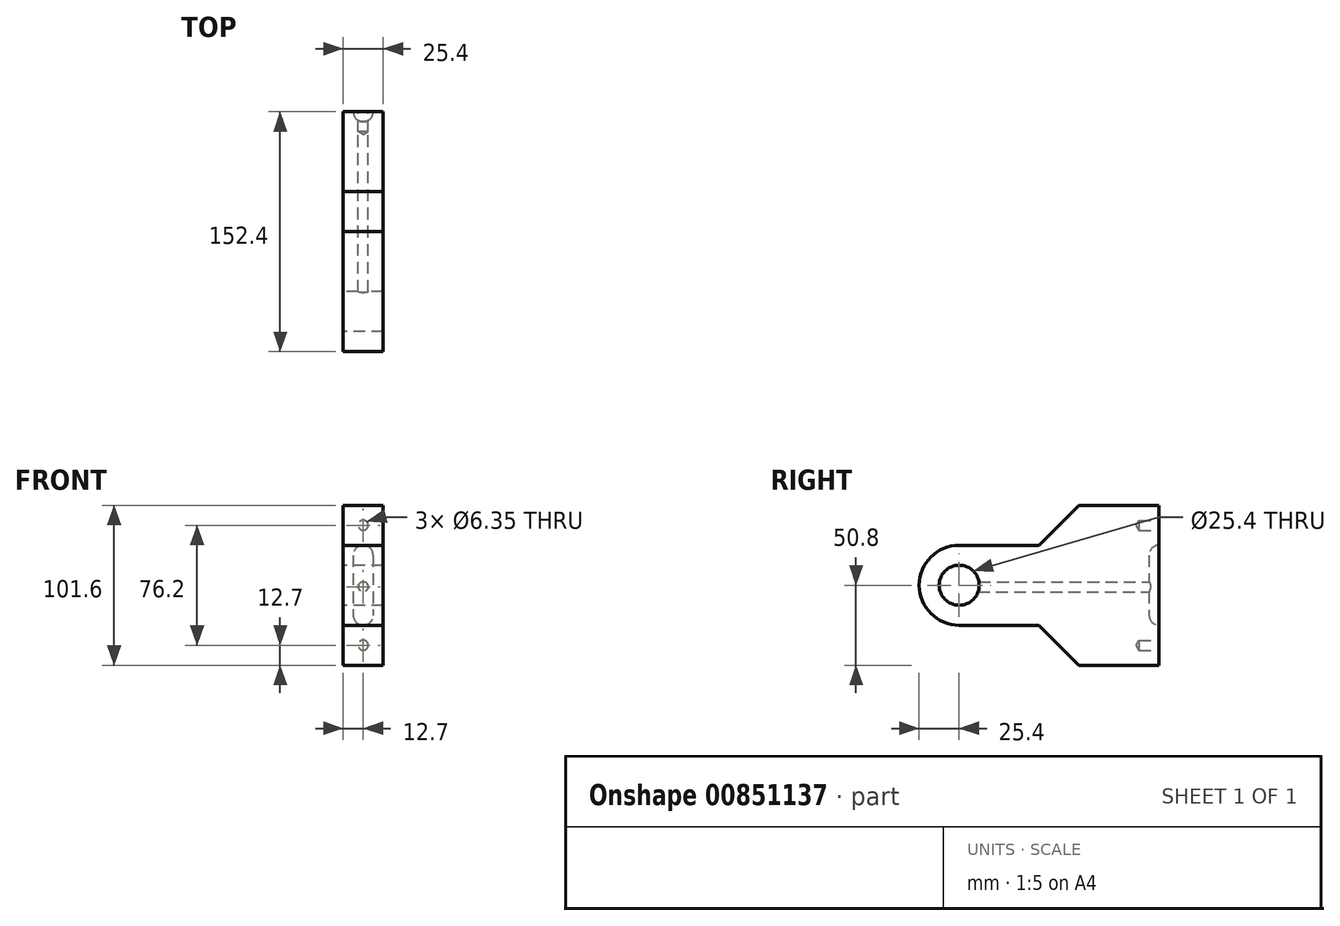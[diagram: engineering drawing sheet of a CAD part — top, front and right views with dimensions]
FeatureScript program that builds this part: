
annotation { "Feature Type Name" : "Feature", "Feature Type Description" : "" }
export const myFeature = defineFeature(function(context is Context, id is Id, definition is map)
    precondition{}
    {
        {
            var Q0;
            Q0=qCreatedBy(makeId("Right.planeOp"),FACE);
            var sketch = newSketch(context, id + "F0", { "sketchPlane" : qUnion([Q0])});
            skLineSegment(sketch, "E0.top", {"start": v(0, 50.8) * mm, "end": v(50.8, 50.8) * mm});
            skArc(sketch, "E1", {"start": v(0, 50.8) * mm, "mid": v(-25.4, 25.4) * mm, "end": v(0, 0) * mm});
            skLineSegment(sketch, "E2", {"start": v(50.8, 50.8) * mm, "end": v(76.2, 76.2) * mm});
            skLineSegment(sketch, "E3", {"start": v(76.2, 76.2) * mm, "end": v(127, 76.2) * mm});
            skLineSegment(sketch, "E4", {"start": v(127, 76.2) * mm, "end": v(127, -25.4) * mm});
            skCircle(sketch, "E5", {"center": v(0, 25.4) * mm, "radius": 12.7 * mm});
            skLineSegment(sketch, "E6", {"start": v(0, 0) * mm, "end": v(50.8, 0) * mm});
            skLineSegment(sketch, "E7", {"start": v(50.8, 0) * mm, "end": v(76.2, -25.4) * mm});
            skLineSegment(sketch, "E8", {"start": v(76.2, -25.4) * mm, "end": v(127, -25.4) * mm});
            skSolve(sketch);
        }
        {
            var Q0;
            Q0=makeQuery(id+"F0.imprint","IMPRINT",FACE,{"disambiguationData":[TD([[makeQuery(id+"F0.imprint","IMPRINT",EDGE,{"derivedFrom":sQuery(id+"F0.wireOp",EDGE,"E0.top")}),-1.0]])]});
            extrude(context, id + "F1", {"entities" : qUnion([Q0]), "depth" : 25.4 * mm, "offsetDistance" : 25.4 * mm});
        }
        {
            var Q0;
            Q0=makeQuery(id+"F1.opExtrude","SWEPT_FACE",FACE,{"disambiguationData":[OSD([sQuery(id+"F0.wireOp",EDGE,"E4")])]});
            var sketch = newSketch(context, id + "F2", { "sketchPlane" : qUnion([Q0])});
            skLineSegment(sketch, "E9.left", {"start": v(-19.05, 44.45) * mm, "end": v(-19.05, 6.35) * mm});
            skArc(sketch, "E10", {"start": v(-19.05, 6.35) * mm, "mid": v(-17.2, 1.86) * mm, "end": v(-12.7, 0) * mm});
            skArc(sketch, "E11", {"start": v(-12.7, 50.8) * mm, "mid": v(-17.2, 48.94) * mm, "end": v(-19.05, 44.45) * mm});
            skLineSegment(sketch, "E12", {"start": v(-12.7, 50.8) * mm, "end": v(-12.7, 0) * mm});
            skSolve(sketch);
        }
        {
            var Q0;
            Q0=makeQuery(id+"F2.imprint","IMPRINT",FACE,{"disambiguationData":[TD([[makeQuery(id+"F2.imprint","IMPRINT",EDGE,{"derivedFrom":sQuery(id+"F2.wireOp",EDGE,"E9.left")}),1.0]])]});
            var Q1;
            Q1=sQuery(id+"F2.wireOp",EDGE,"E12");
            revolve(context, id + "F3", {"operationType" : NewBodyOperationType.REMOVE, "surfaceOperationType" : NewSurfaceOperationType.NEW, "entities" : qUnion([Q0]), "axis" : qUnion([Q1]), "revolveType" : RevolveType.FULL, "oppositeDirection" : true});
        }
        {
            var Q0;
            Q0=makeQuery(id+"F1.opExtrude","SWEPT_FACE",FACE,{"disambiguationData":[OSD([sQuery(id+"F0.wireOp",EDGE,"E4")])]});
            var sketch = newSketch(context, id + "F4", { "sketchPlane" : qUnion([Q0])});
            skPoint(sketch, "E13.centerSnap0", {"position": v(-12.7, 12.7) * mm});
            skPoint(sketch, "E14.centerSnap0", {"position": v(-12.7, 50.8) * mm});
            skPoint(sketch, "E15", {"position": v(-12.7, 63.5) * mm});
            skPoint(sketch, "E16", {"position": v(-12.7, -12.7) * mm});
            skPoint(sketch, "E16.positionSnap0", {"position": v(-12.7, 0) * mm});
            skSolve(sketch);
        }
        {
            var Q0;
            Q0=sQuery(id+"F4.wireOp",VERTEX,"E15");
            var Q1;
            Q1=sQuery(id+"F4.wireOp",VERTEX,"E16");
            var Q2;
            Q2=makeQuery(id+"F1.opExtrude","SWEPT_BODY",BODY,{"disambiguationData":[OSD([sQuery(id+"F0.wireOp",EDGE,"E0.top"),sQuery(id+"F0.wireOp",EDGE,"E1"),sQuery(id+"F0.wireOp",EDGE,"E2"),sQuery(id+"F0.wireOp",EDGE,"E3"),sQuery(id+"F0.wireOp",EDGE,"E4"),sQuery(id+"F0.wireOp",EDGE,"E5"),sQuery(id+"F0.wireOp",EDGE,"E6"),sQuery(id+"F0.wireOp",EDGE,"E7"),sQuery(id+"F0.wireOp",EDGE,"E8")])]});
            hole(context, id + "F5", {"style" : HoleStyle.SIMPLE, "endStyle" : HoleEndStyle.BLIND, "holeDiameter" : 6.35 * mm, "majorDiameter" : 6.35 * mm, "holeDepth" : 12.7 * mm, "isTappedThrough" : true, "tappedDepth" : 12.7 * mm, "tapClearance" : 3, "locations" : qUnion([Q0, Q1]), "scope" : qUnion([Q2])});
        }
        {
            var Q0;
            Q0=makeQuery(id+"F1.opExtrude","SWEPT_FACE",FACE,{"disambiguationData":[OSD([sQuery(id+"F0.wireOp",EDGE,"E4")])]});
            var sketch = newSketch(context, id + "F6", { "sketchPlane" : qUnion([Q0])});
            skPoint(sketch, "E17", {"position": v(-12.7, 24.42) * mm});
            skPoint(sketch, "E17.positionSnap0", {"position": v(-12.7, 50.8) * mm});
            skSolve(sketch);
        }
        {
            var Q0;
            Q0=sQuery(id+"F6.wireOp",VERTEX,"E17");
            var Q1;
            Q1=makeQuery(id+"F1.opExtrude","SWEPT_BODY",BODY,{"disambiguationData":[OSD([sQuery(id+"F0.wireOp",EDGE,"E0.top"),sQuery(id+"F0.wireOp",EDGE,"E1"),sQuery(id+"F0.wireOp",EDGE,"E2"),sQuery(id+"F0.wireOp",EDGE,"E3"),sQuery(id+"F0.wireOp",EDGE,"E4"),sQuery(id+"F0.wireOp",EDGE,"E5"),sQuery(id+"F0.wireOp",EDGE,"E6"),sQuery(id+"F0.wireOp",EDGE,"E7"),sQuery(id+"F0.wireOp",EDGE,"E8")])]});
            hole(context, id + "F7", {"style" : HoleStyle.SIMPLE, "endStyle" : HoleEndStyle.BLIND, "holeDiameter" : 6.35 * mm, "majorDiameter" : 6.35 * mm, "holeDepth" : 127 * mm, "isTappedThrough" : true, "tappedDepth" : 12.7 * mm, "tapClearance" : 3, "locations" : qUnion([Q0]), "scope" : qUnion([Q1])});
        }
    });
